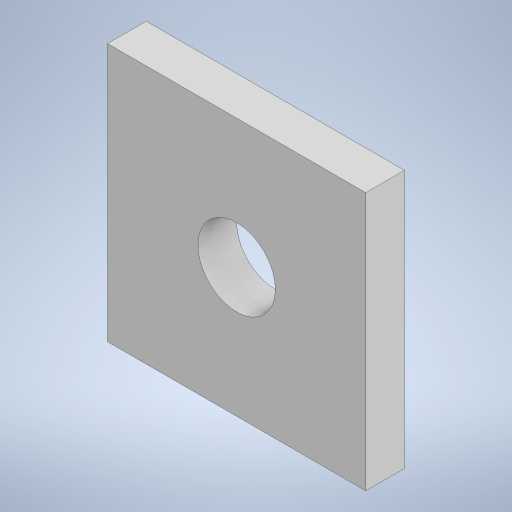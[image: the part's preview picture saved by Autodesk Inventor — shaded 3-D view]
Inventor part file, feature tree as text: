
AUTODESK INVENTOR PART (.ipt)
format: ipt  version: 2023 (Build 270158000, 158)  size: 222,720 bytes
history: native  units: mm
features: extrude x2, sketch x2
ambient origin geometry x8: Origin, YZ Plane, XZ Plane, XY Plane, X Axis, Y Axis, Z Axis, Center Point
bodies: Body1 (feature_tree)
feature tree (4):
  extrude  "Extrusion45"  Depth=20.0mm
  extrude  "Extrusion46"  Depth=3.0mm
  sketch  "Sketch66"  dims[d179=20.0mm d180=20.0mm]
  sketch  "Sketch67"  dims[d181=3.0mm d182=0.0mm d183=6.0mm d184=3.0mm d185=0.0mm d49=0.5mm d50=0.872665mm d51=0.5mm d52=0.872665mm d130=0.5mm d131=0.872665mm d132=0.5mm d133=0.872665mm d156=0.5mm d157=0.872665mm d158=0.5mm d159=0.872665mm]
